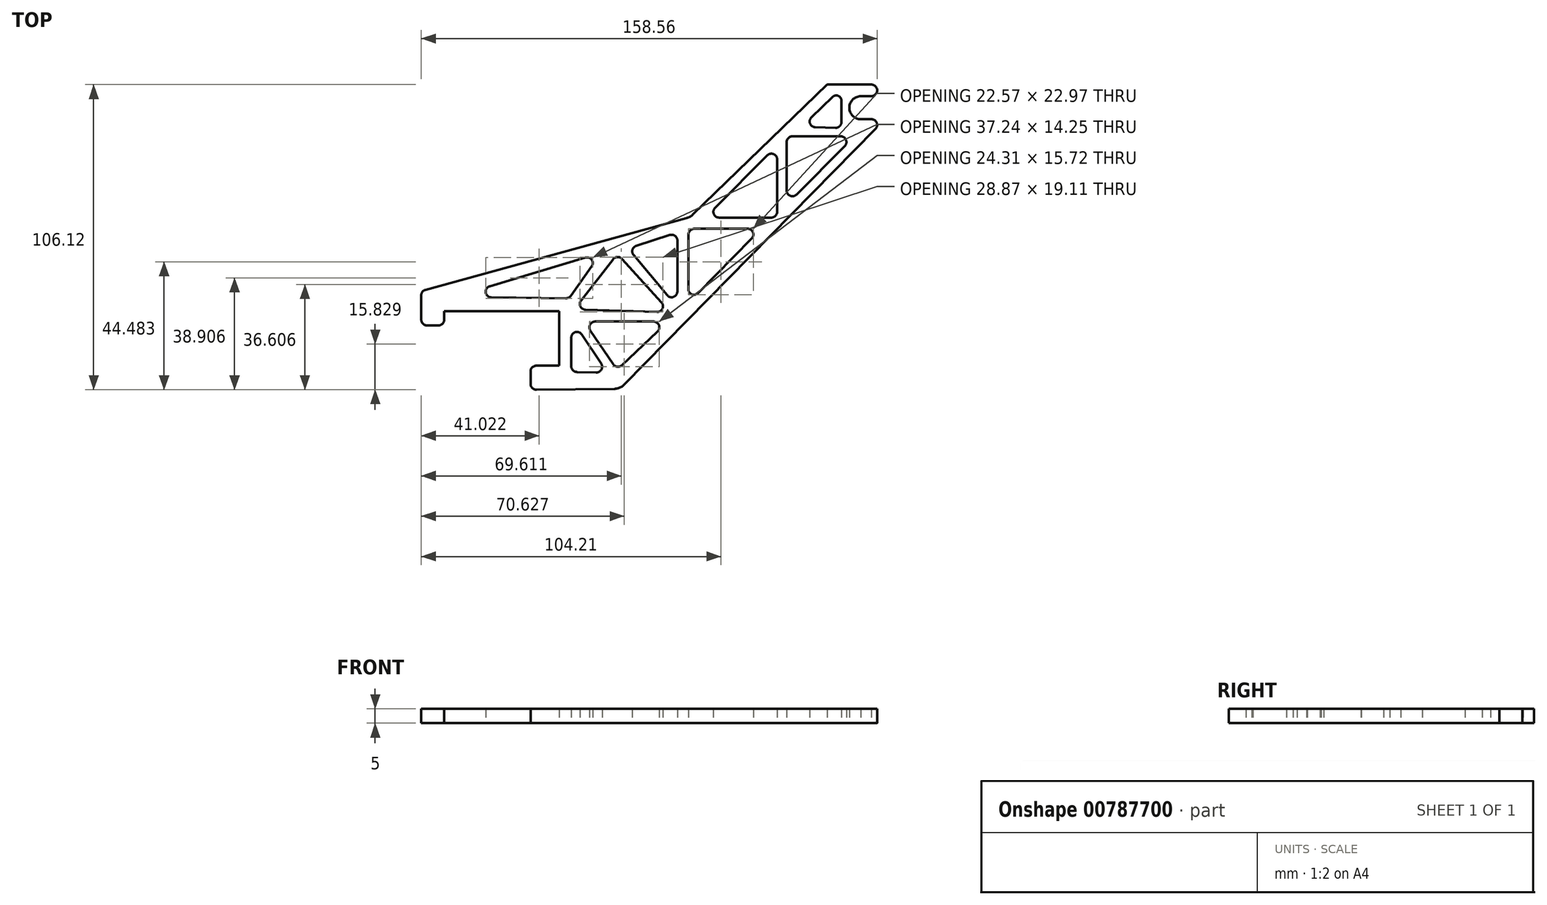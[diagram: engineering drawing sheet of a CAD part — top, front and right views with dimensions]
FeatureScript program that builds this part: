
annotation { "Feature Type Name" : "Feature", "Feature Type Description" : "" }
export const myFeature = defineFeature(function(context is Context, id is Id, definition is map)
    precondition{}
    {
        {
            var Q0;
            Q0=qCreatedBy(makeId("Top.planeOp"),FACE);
            var sketch = newSketch(context, id + "F0", { "sketchPlane" : qUnion([Q0])});
            skLineSegment(sketch, "E0", {"start": v(0.84, -52.88) * mm, "end": v(88.2, 36.01) * mm});
            skLineSegment(sketch, "E1", {"start": v(76.08, 33.46) * mm, "end": v(59.28, 33.46) * mm});
            skLineSegment(sketch, "E2", {"start": v(57.28, 31.46) * mm, "end": v(57.28, 14.61) * mm});
            skLineSegment(sketch, "E3", {"start": v(52, 5.19) * mm, "end": v(33.8, 5.19) * mm});
            skLineSegment(sketch, "E4", {"start": v(32.4, 8.6) * mm, "end": v(50.58, 26.85) * mm});
            skLineSegment(sketch, "E5", {"start": v(43.71, 1.3) * mm, "end": v(25.14, 1.3) * mm});
            skLineSegment(sketch, "E6", {"start": v(23.14, -0.7) * mm, "end": v(23.14, -19.78) * mm});
            skLineSegment(sketch, "E7", {"start": v(19.27, -20.53) * mm, "end": v(19.27, -2.77) * mm});
            skLineSegment(sketch, "E8", {"start": v(16.66, -0.86) * mm, "end": v(4.97, -4.64) * mm});
            skLineSegment(sketch, "E9", {"start": v(4.05, -7.83) * mm, "end": v(15.74, -21.81) * mm});
            skLineSegment(sketch, "E10", {"start": v(26.39, -21.11) * mm, "end": v(45.14, -2.1) * mm});
            skLineSegment(sketch, "E11", {"start": v(-12.69, -26.86) * mm, "end": v(12.22, -27.62) * mm});
            skLineSegment(sketch, "E12", {"start": v(-9.32, -30.98) * mm, "end": v(11, -30.98) * mm});
            skLineSegment(sketch, "E13", {"start": v(12.37, -34.43) * mm, "end": v(0, -46.16) * mm});
            skLineSegment(sketch, "E14", {"start": v(-3.03, -45.83) * mm, "end": v(-10.98, -34.1) * mm});
            skLineSegment(sketch, "E15", {"start": v(-17.83, -22.05) * mm, "end": v(-10.52, -11.8) * mm});
            skLineSegment(sketch, "E16", {"start": v(-12.72, -8.72) * mm, "end": v(-45.98, -18.68) * mm});
            skLineSegment(sketch, "E17", {"start": v(-45.43, -22.6) * mm, "end": v(-19.48, -22.9) * mm});
            skLineSegment(sketch, "E18", {"start": v(-69.78, -21.7) * mm, "end": v(-69.79, -30.33) * mm});
            skLineSegment(sketch, "E19", {"start": v(-67.79, -32.33) * mm, "end": v(-63.79, -32.33) * mm});
            skLineSegment(sketch, "E20", {"start": v(-61.79, -30.33) * mm, "end": v(-61.79, -27.33) * mm});
            skLineSegment(sketch, "E21", {"start": v(-61.79, -27.33) * mm, "end": v(-21.79, -27.33) * mm});
            skLineSegment(sketch, "E22", {"start": v(-21.79, -27.33) * mm, "end": v(-21.79, -46.33) * mm});
            skLineSegment(sketch, "E23", {"start": v(-21.79, -46.33) * mm, "end": v(-29.79, -46.33) * mm});
            skLineSegment(sketch, "E24", {"start": v(-31.79, -48.33) * mm, "end": v(-31.79, -52.67) * mm});
            skLineSegment(sketch, "E25", {"start": v(-2.67, -54.37) * mm, "end": v(-29.77, -54.67) * mm});
            skLineSegment(sketch, "E26", {"start": v(22.55, 5.05) * mm, "end": v(-68.46, -19.97) * mm});
            skLineSegment(sketch, "E27", {"start": v(-69.78, -20.33) * mm, "end": v(-69.78, -20.33) * mm});
            skLineSegment(sketch, "E28", {"start": v(24.7, 6.28) * mm, "end": v(71.39, 51.45) * mm});
            skLineSegment(sketch, "E29", {"start": v(83.1, 39.41) * mm, "end": v(86.77, 39.41) * mm});
            skLineSegment(sketch, "E30", {"start": v(83.1, 47.41) * mm, "end": v(86.77, 47.45) * mm});
            skLineSegment(sketch, "E31", {"start": v(-7.23, -45.57) * mm, "end": v(-13.96, -35.47) * mm});
            skLineSegment(sketch, "E32", {"start": v(-17.62, -36.58) * mm, "end": v(-17.62, -46.51) * mm});
            skLineSegment(sketch, "E33", {"start": v(-15.67, -48.51) * mm, "end": v(-8.94, -48.68) * mm});
            skLineSegment(sketch, "E34", {"start": v(54, 25.43) * mm, "end": v(54, 7.19) * mm});
            skLineSegment(sketch, "E35", {"start": v(77.5, 30.05) * mm, "end": v(60.7, 13.2) * mm});
            skLineSegment(sketch, "E36", {"start": v(76.34, 38.4) * mm, "end": v(76.34, 45.88) * mm});
            skLineSegment(sketch, "E37", {"start": v(73.29, 47.17) * mm, "end": v(65.91, 40.04) * mm});
            skLineSegment(sketch, "E38", {"start": v(67.25, 36.6) * mm, "end": v(74.29, 36.4) * mm});
            skLineSegment(sketch, "E39", {"start": v(0, -9.16) * mm, "end": v(13.76, -24.27) * mm});
            skLineSegment(sketch, "E40", {"start": v(-3.06, -9.28) * mm, "end": v(-14.2, -23.63) * mm});
            skPoint(sketch, "E41.visualSharp", {"position": v(76.34, 36.35) * mm});
            skArc(sketch, "E41.filletArc", {"start": v(74.29, 36.4) * mm, "mid": v(75.74, 36.97) * mm, "end": v(76.34, 38.4) * mm});
            skPoint(sketch, "E42.visualSharp", {"position": v(80.9, 33.46) * mm});
            skArc(sketch, "E42.filletArc", {"start": v(77.5, 30.05) * mm, "mid": v(77.93, 32.23) * mm, "end": v(76.08, 33.46) * mm});
            skPoint(sketch, "E43.visualSharp", {"position": v(57.28, 33.46) * mm});
            skArc(sketch, "E43.filletArc", {"start": v(59.28, 33.46) * mm, "mid": v(57.87, 32.88) * mm, "end": v(57.28, 31.46) * mm});
            skPoint(sketch, "E44.visualSharp", {"position": v(57.28, 9.77) * mm});
            skArc(sketch, "E44.filletArc", {"start": v(57.28, 14.61) * mm, "mid": v(58.52, 12.76) * mm, "end": v(60.7, 13.2) * mm});
            skArc(sketch, "E45.filletArc", {"start": v(65.91, 40.04) * mm, "mid": v(65.44, 37.87) * mm, "end": v(67.25, 36.6) * mm});
            skArc(sketch, "E46.filletArc", {"start": v(76.34, 45.88) * mm, "mid": v(75.24, 47.54) * mm, "end": v(73.29, 47.17) * mm});
            skPoint(sketch, "E47.visualSharp", {"position": v(54, 30.27) * mm});
            skArc(sketch, "E47.filletArc", {"start": v(54, 25.43) * mm, "mid": v(52.76, 27.28) * mm, "end": v(50.58, 26.85) * mm});
            skPoint(sketch, "E48.visualSharp", {"position": v(54, 5.19) * mm});
            skArc(sketch, "E48.filletArc", {"start": v(52, 5.19) * mm, "mid": v(53.41, 5.77) * mm, "end": v(54, 7.19) * mm});
            skPoint(sketch, "E49.visualSharp", {"position": v(28.99, 5.19) * mm});
            skArc(sketch, "E49.filletArc", {"start": v(32.4, 8.6) * mm, "mid": v(31.96, 6.42) * mm, "end": v(33.8, 5.19) * mm});
            skPoint(sketch, "E50.visualSharp", {"position": v(23.14, 1.3) * mm});
            skArc(sketch, "E50.filletArc", {"start": v(25.14, 1.3) * mm, "mid": v(23.72, 0.71) * mm, "end": v(23.14, -0.7) * mm});
            skPoint(sketch, "E51.visualSharp", {"position": v(48.5, 1.3) * mm});
            skArc(sketch, "E51.filletArc", {"start": v(45.14, -2.1) * mm, "mid": v(45.56, 0.07) * mm, "end": v(43.71, 1.3) * mm});
            skPoint(sketch, "E52.visualSharp", {"position": v(23.14, -24.41) * mm});
            skArc(sketch, "E52.filletArc", {"start": v(23.14, -19.78) * mm, "mid": v(24.32, -21.54) * mm, "end": v(26.39, -21.11) * mm});
            skPoint(sketch, "E53.visualSharp", {"position": v(19.27, -26.05) * mm});
            skArc(sketch, "E53.filletArc", {"start": v(15.74, -21.81) * mm, "mid": v(17.95, -22.41) * mm, "end": v(19.27, -20.53) * mm});
            skPoint(sketch, "E54.visualSharp", {"position": v(19.27, -0.02) * mm});
            skArc(sketch, "E54.filletArc", {"start": v(19.27, -2.77) * mm, "mid": v(18.45, -1.15) * mm, "end": v(16.66, -0.86) * mm});
            skPoint(sketch, "E55.visualSharp", {"position": v(2.15, -5.55) * mm});
            skArc(sketch, "E55.filletArc", {"start": v(4.97, -4.64) * mm, "mid": v(3.67, -5.99) * mm, "end": v(4.05, -7.83) * mm});
            skPoint(sketch, "E56.visualSharp", {"position": v(-1.6, -7.4) * mm});
            skArc(sketch, "E56.filletArc", {"start": v(0, -9.16) * mm, "mid": v(-1.56, -8.51) * mm, "end": v(-3.06, -9.28) * mm});
            skPoint(sketch, "E57.visualSharp", {"position": v(16.93, -27.76) * mm});
            skArc(sketch, "E57.filletArc", {"start": v(12.22, -27.62) * mm, "mid": v(14.1, -26.45) * mm, "end": v(13.76, -24.27) * mm});
            skPoint(sketch, "E58.visualSharp", {"position": v(-16.62, -26.74) * mm});
            skArc(sketch, "E58.filletArc", {"start": v(-14.2, -23.63) * mm, "mid": v(-14.44, -25.71) * mm, "end": v(-12.69, -26.86) * mm});
            skPoint(sketch, "E59.visualSharp", {"position": v(-13.09, -30.98) * mm});
            skArc(sketch, "E59.filletArc", {"start": v(-9.32, -30.98) * mm, "mid": v(-11.09, -32.05) * mm, "end": v(-10.98, -34.1) * mm});
            skPoint(sketch, "E60.visualSharp", {"position": v(16.01, -30.98) * mm});
            skArc(sketch, "E60.filletArc", {"start": v(12.37, -34.43) * mm, "mid": v(12.86, -32.24) * mm, "end": v(11, -30.98) * mm});
            skPoint(sketch, "E61.visualSharp", {"position": v(-1.71, -47.78) * mm});
            skArc(sketch, "E61.filletArc", {"start": v(-3.03, -45.83) * mm, "mid": v(-1.6, -46.7) * mm, "end": v(0, -46.16) * mm});
            skPoint(sketch, "E62.visualSharp", {"position": v(-5.1, -48.77) * mm});
            skArc(sketch, "E62.filletArc", {"start": v(-8.94, -48.68) * mm, "mid": v(-7.14, -47.64) * mm, "end": v(-7.23, -45.57) * mm});
            skPoint(sketch, "E63.visualSharp", {"position": v(-17.62, -48.47) * mm});
            skArc(sketch, "E63.filletArc", {"start": v(-17.62, -46.51) * mm, "mid": v(-17.05, -47.91) * mm, "end": v(-15.67, -48.51) * mm});
            skPoint(sketch, "E64.visualSharp", {"position": v(-17.62, -29.97) * mm});
            skArc(sketch, "E64.filletArc", {"start": v(-13.96, -35.47) * mm, "mid": v(-16.2, -34.66) * mm, "end": v(-17.62, -36.58) * mm});
            skPoint(sketch, "E65.visualSharp", {"position": v(-18.43, -22.9) * mm});
            skArc(sketch, "E65.filletArc", {"start": v(-19.48, -22.9) * mm, "mid": v(-18.55, -22.67) * mm, "end": v(-17.83, -22.05) * mm});
            skPoint(sketch, "E66.visualSharp", {"position": v(-7.14, -7.05) * mm});
            skArc(sketch, "E66.filletArc", {"start": v(-10.52, -11.8) * mm, "mid": v(-10.52, -9.47) * mm, "end": v(-12.72, -8.72) * mm});
            skPoint(sketch, "E67.visualSharp", {"position": v(-58.56, -22.44) * mm});
            skArc(sketch, "E67.filletArc", {"start": v(-45.98, -18.68) * mm, "mid": v(-47.39, -20.87) * mm, "end": v(-45.43, -22.6) * mm});
            skPoint(sketch, "E68.visualSharp", {"position": v(-31.79, -46.33) * mm});
            skArc(sketch, "E68.filletArc", {"start": v(-29.79, -46.33) * mm, "mid": v(-31.2, -46.92) * mm, "end": v(-31.79, -48.33) * mm});
            skPoint(sketch, "E69.visualSharp", {"position": v(-31.79, -54.7) * mm});
            skArc(sketch, "E69.filletArc", {"start": v(-31.79, -52.67) * mm, "mid": v(-31.2, -54.1) * mm, "end": v(-29.77, -54.67) * mm});
            skPoint(sketch, "E70.visualSharp", {"position": v(-69.79, -32.33) * mm});
            skArc(sketch, "E70.filletArc", {"start": v(-69.79, -30.33) * mm, "mid": v(-69.2, -31.75) * mm, "end": v(-67.79, -32.33) * mm});
            skPoint(sketch, "E71.visualSharp", {"position": v(-69.78, -20.33) * mm});
            skArc(sketch, "E71.filletArc", {"start": v(-68.46, -19.97) * mm, "mid": v(-69.41, -20.6) * mm, "end": v(-69.78, -21.7) * mm});
            skPoint(sketch, "E72.visualSharp", {"position": v(-0.6, -54.35) * mm});
            skArc(sketch, "E72.filletArc", {"start": v(-2.67, -54.37) * mm, "mid": v(-0.77, -53.97) * mm, "end": v(0.84, -52.88) * mm});
            skPoint(sketch, "E73.visualSharp", {"position": v(23.78, 5.39) * mm});
            skArc(sketch, "E73.filletArc", {"start": v(22.55, 5.05) * mm, "mid": v(23.7, 5.53) * mm, "end": v(24.7, 6.28) * mm});
            skPoint(sketch, "E74.visualSharp", {"position": v(91.54, 39.41) * mm});
            skArc(sketch, "E74.filletArc", {"start": v(88.2, 36.01) * mm, "mid": v(88.61, 38.19) * mm, "end": v(86.77, 39.41) * mm});
            skPoint(sketch, "E75.visualSharp", {"position": v(-61.79, -32.33) * mm});
            skArc(sketch, "E75.filletArc", {"start": v(-63.79, -32.33) * mm, "mid": v(-62.37, -31.75) * mm, "end": v(-61.79, -30.33) * mm});
            skLineSegment(sketch, "E76", {"start": v(71.39, 51.45) * mm, "end": v(86.77, 51.45) * mm});
            skArc(sketch, "E77", {"start": v(83.1, 47.41) * mm, "mid": v(79.1, 43.41) * mm, "end": v(83.1, 39.41) * mm});
            skArc(sketch, "E78", {"start": v(86.77, 47.45) * mm, "mid": v(88.77, 49.45) * mm, "end": v(86.77, 51.45) * mm});
            skSolve(sketch);
        }
        {
            var Q0;
            Q0 = qSketchRegion(id + "F0", true);
            extrude(context, id + "F1", {"entities" : qUnion([Q0]), "depth" : 5 * mm, "offsetDistance" : 25 * mm});
        }
    });
